# Revit family: Dining_Bench_Petit_BIM
name_source: partatom
category: Arredi
units: mm (PartAtom-declared; Revit-internal decimal feet)

## family parameters
Attiva taglio nelle viste = No
Basato su piano di lavoro = No
Condiviso = No
Numero OmniClass = 23.40.20.00
Origine composizione di rendering = Geometria famiglia
Punto di calcolo locali = No
Sempre verticale = Sì
Taglio con vuoti quando caricato = No
Titolo OmniClass = General Furniture and Specialties

## types (1)
- CB-40
    AVAILABLE FINISHES = Ebonized black lacquer on Ash (EB) or bleached, white pigment, matte acrylic on Ash (BL). Raw effect lacquer on Oak (RE). Hand rubbed natural oil on Oak or Walnut (NA), or hand rubbed black oil on Walnut (BO). Hand rubbed outdoor oil with UV protection on Teak (NA).
    BASE MATERIAL = BASSAM_FELLOWS_WALNUT_BLACK_OIL_W-BO
    BIM BADGE = https://bim.archiproducts.com
    COLLECTION = Dining Bench
    DEPTH = 440 mm  [stored 1.44357 ft]
    Descrizione = Upholstered leather and solid wood dining bench
    HEIGHT = 450 mm
    MATERIAL DESCRIPTION = Solid wood frame. Solid wood seat slats. Dual density upholstery foam with edge banding, topped with feather and down. Inverted seam detail.
    Modello = Dining Bench Petit
    PRODUCT CODE = CB-40
    PRODUCT SHEET = https://www.archiproducts.com
    Produttore = BassamFellows
    Prospetto di default = 0 mm  [stored 0 ft]
    TECHNICAL SHEET = https://bassamfellows.com
    UPHOLSTERY MATERIAL = BASSAM_FELLOWS_COMFORT_LEATHER_02067_BEIGE
    URL = https://bassamfellows.com
    WIDTH = 1640 mm

note: [stored X ft] marks values corroborated as IEEE doubles in the binary element streams (Revit-internal decimal feet)

## geometry (parser evidence)
native form markers: Sweep x2
no freeform markers — native parametric forms only
